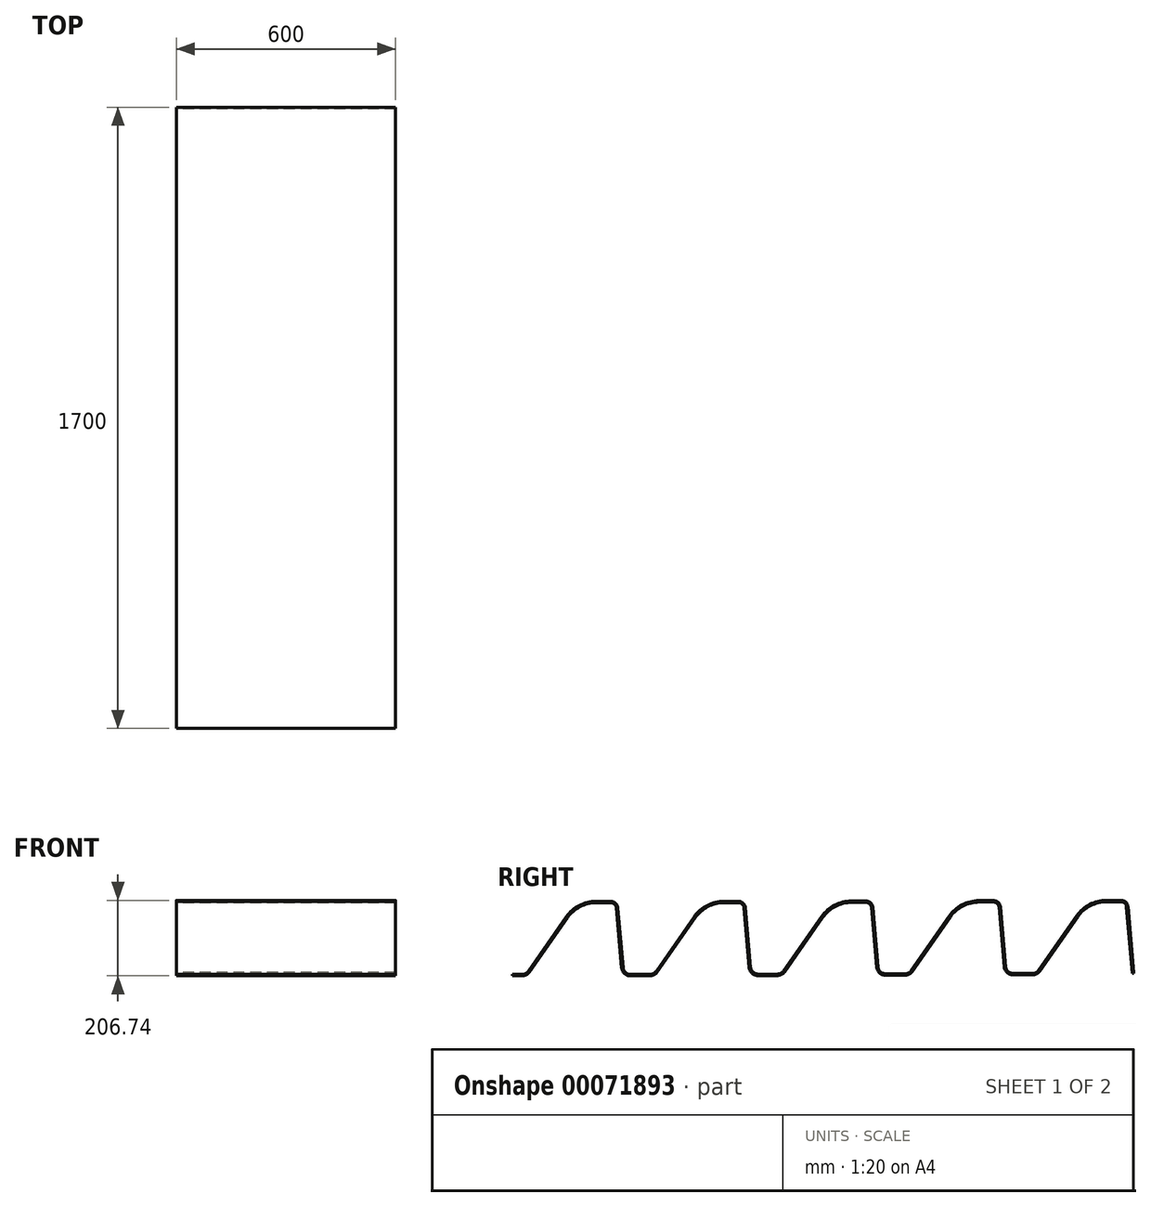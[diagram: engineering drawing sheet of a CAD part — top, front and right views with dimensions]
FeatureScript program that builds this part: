
annotation { "Feature Type Name" : "Feature", "Feature Type Description" : "" }
export const myFeature = defineFeature(function(context is Context, id is Id, definition is map)
    precondition{}
    {
        {
            var Q0;
            Q0=qCreatedBy(makeId("Right.planeOp"),FACE);
            var sketch = newSketch(context, id + "F0", { "sketchPlane" : qUnion([Q0])});
            skLineSegment(sketch, "E0", {"start": v(5.97, 8.53) * mm, "end": v(110.18, 157.36) * mm});
            skLineSegment(sketch, "E1", {"start": v(192.1, 200) * mm, "end": v(231.67, 200) * mm});
            skPoint(sketch, "E2.visualSharp", {"position": v(140.04, 200) * mm});
            skArc(sketch, "E2.filletArc", {"start": v(192.1, 200) * mm, "mid": v(145.92, 188.7) * mm, "end": v(110.18, 157.36) * mm});
            skLineSegment(sketch, "E3", {"start": v(251.6, 181.74) * mm, "end": v(265.9, 18.26) * mm});
            skPoint(sketch, "E4.visualSharp", {"position": v(250, 200) * mm});
            skArc(sketch, "E4.filletArc", {"start": v(251.6, 181.74) * mm, "mid": v(245.19, 194.75) * mm, "end": v(231.67, 200) * mm});
            skLineSegment(sketch, "E5.1.0.0", {"start": v(600.6, 182.66) * mm, "end": v(614.9, 19.17) * mm});
            skPoint(sketch, "E5.1.0.1", {"position": v(600, 200) * mm});
            skArc(sketch, "E5.1.0.2", {"start": v(542.1, 200) * mm, "mid": v(495.92, 188.7) * mm, "end": v(460.18, 157.36) * mm});
            skPoint(sketch, "E5.1.0.3", {"position": v(490.04, 200) * mm});
            skLineSegment(sketch, "E5.1.0.5", {"start": v(542.1, 200) * mm, "end": v(581.67, 200) * mm});
            skLineSegment(sketch, "E5.1.0.6", {"start": v(355.97, 8.53) * mm, "end": v(460.18, 157.36) * mm});
            skArc(sketch, "E5.1.0.7", {"start": v(600.6, 182.66) * mm, "mid": v(594.5, 195) * mm, "end": v(581.67, 200) * mm});
            skLineSegment(sketch, "E5.2.0.0", {"start": v(949.6, 183.57) * mm, "end": v(963.9, 20.08) * mm});
            skPoint(sketch, "E5.2.0.1", {"position": v(950, 200) * mm});
            skArc(sketch, "E5.2.0.2", {"start": v(891.1, 200.91) * mm, "mid": v(844.93, 189.61) * mm, "end": v(809.19, 158.27) * mm});
            skPoint(sketch, "E5.2.0.3", {"position": v(840.04, 200) * mm});
            skLineSegment(sketch, "E5.2.0.5", {"start": v(891.1, 200.91) * mm, "end": v(930.68, 200.91) * mm});
            skLineSegment(sketch, "E5.2.0.6", {"start": v(704.98, 9.44) * mm, "end": v(809.19, 158.27) * mm});
            skArc(sketch, "E5.2.0.7", {"start": v(949.6, 183.57) * mm, "mid": v(943.51, 195.92) * mm, "end": v(930.68, 200.91) * mm});
            skLineSegment(sketch, "E5.3.0.0", {"start": v(1298.6, 184.48) * mm, "end": v(1312.91, 21) * mm});
            skPoint(sketch, "E5.3.0.1", {"position": v(1300, 200) * mm});
            skArc(sketch, "E5.3.0.2", {"start": v(1240.1, 201.83) * mm, "mid": v(1193.93, 190.53) * mm, "end": v(1158.2, 159.18) * mm});
            skPoint(sketch, "E5.3.0.3", {"position": v(1190.04, 200) * mm});
            skLineSegment(sketch, "E5.3.0.5", {"start": v(1240.1, 201.83) * mm, "end": v(1279.68, 201.83) * mm});
            skLineSegment(sketch, "E5.3.0.6", {"start": v(1053.98, 10.35) * mm, "end": v(1158.2, 159.18) * mm});
            skArc(sketch, "E5.3.0.7", {"start": v(1298.6, 184.48) * mm, "mid": v(1292.52, 196.83) * mm, "end": v(1279.68, 201.83) * mm});
            skLineSegment(sketch, "E5.4.0.0", {"start": v(1647.61, 185.4) * mm, "end": v(1663.4, 5.01) * mm});
            skPoint(sketch, "E5.4.0.1", {"position": v(1650, 200) * mm});
            skArc(sketch, "E5.4.0.2", {"start": v(1589.1, 202.74) * mm, "mid": v(1542.93, 191.44) * mm, "end": v(1507.2, 160.1) * mm});
            skPoint(sketch, "E5.4.0.3", {"position": v(1540.04, 200) * mm});
            skLineSegment(sketch, "E5.4.0.5", {"start": v(1589.1, 202.74) * mm, "end": v(1628.68, 202.74) * mm});
            skLineSegment(sketch, "E5.4.0.6", {"start": v(1402.98, 11.27) * mm, "end": v(1507.2, 160.1) * mm});
            skArc(sketch, "E5.4.0.7", {"start": v(1647.61, 185.4) * mm, "mid": v(1641.52, 197.75) * mm, "end": v(1628.68, 202.74) * mm});
            skLineSegment(sketch, "E6", {"start": v(1332.84, 2.74) * mm, "end": v(1386.6, 2.74) * mm});
            skLineSegment(sketch, "E7", {"start": v(983.83, 1.83) * mm, "end": v(1037.6, 1.83) * mm});
            skLineSegment(sketch, "E8", {"start": v(634.83, 0.91) * mm, "end": v(688.6, 0.91) * mm});
            skLineSegment(sketch, "E9", {"start": v(285.82, 0) * mm, "end": v(339.59, 0) * mm});
            skLineSegment(sketch, "E10", {"start": v(-10.41, 0) * mm, "end": v(-36.6, 0) * mm});
            skPoint(sketch, "E11.visualSharp", {"position": v(267.5, 0) * mm});
            skArc(sketch, "E11.filletArc", {"start": v(265.9, 18.26) * mm, "mid": v(272.31, 5.25) * mm, "end": v(285.82, 0) * mm});
            skPoint(sketch, "E12.visualSharp", {"position": v(350, 0) * mm});
            skArc(sketch, "E12.filletArc", {"start": v(339.59, 0) * mm, "mid": v(348.82, 2.26) * mm, "end": v(355.97, 8.53) * mm});
            skPoint(sketch, "E13.visualSharp", {"position": v(616.5, 0.91) * mm});
            skArc(sketch, "E13.filletArc", {"start": v(614.9, 19.17) * mm, "mid": v(621.32, 6.17) * mm, "end": v(634.83, 0.91) * mm});
            skPoint(sketch, "E14.visualSharp", {"position": v(699, 0.91) * mm});
            skArc(sketch, "E14.filletArc", {"start": v(688.6, 0.91) * mm, "mid": v(697.83, 3.17) * mm, "end": v(704.98, 9.44) * mm});
            skPoint(sketch, "E15.visualSharp", {"position": v(965.5, 1.83) * mm});
            skArc(sketch, "E15.filletArc", {"start": v(963.9, 20.08) * mm, "mid": v(970.32, 7.08) * mm, "end": v(983.83, 1.83) * mm});
            skPoint(sketch, "E16.visualSharp", {"position": v(1048, 1.83) * mm});
            skArc(sketch, "E16.filletArc", {"start": v(1037.6, 1.83) * mm, "mid": v(1046.83, 4.09) * mm, "end": v(1053.98, 10.35) * mm});
            skPoint(sketch, "E17.visualSharp", {"position": v(1314.5, 2.74) * mm});
            skArc(sketch, "E17.filletArc", {"start": v(1312.91, 21) * mm, "mid": v(1319.32, 8) * mm, "end": v(1332.84, 2.74) * mm});
            skPoint(sketch, "E18.visualSharp", {"position": v(1397.01, 2.74) * mm});
            skArc(sketch, "E18.filletArc", {"start": v(1386.6, 2.74) * mm, "mid": v(1395.84, 5) * mm, "end": v(1402.98, 11.27) * mm});
            skPoint(sketch, "E19.visualSharp", {"position": v(0, 0) * mm});
            skArc(sketch, "E19.filletArc", {"start": v(-10.41, 0) * mm, "mid": v(-1.18, 2.26) * mm, "end": v(5.97, 8.53) * mm});
            skLineSegment(sketch, "E20.0", {"start": v(1643.63, 185.05) * mm, "end": v(1659.53, 3.3) * mm});
            skArc(sketch, "E20.1", {"start": v(1643.63, 185.05) * mm, "mid": v(1638.82, 194.8) * mm, "end": v(1628.68, 198.74) * mm});
            skLineSegment(sketch, "E20.2", {"start": v(1589.1, 198.74) * mm, "end": v(1628.68, 198.74) * mm});
            skArc(sketch, "E20.3", {"start": v(1589.1, 198.74) * mm, "mid": v(1544.78, 187.9) * mm, "end": v(1510.47, 157.8) * mm});
            skLineSegment(sketch, "E20.4", {"start": v(1406.26, 8.97) * mm, "end": v(1510.47, 157.8) * mm});
            skArc(sketch, "E20.5", {"start": v(1386.6, -1.26) * mm, "mid": v(1397.68, 1.45) * mm, "end": v(1406.26, 8.97) * mm});
            skLineSegment(sketch, "E20.6", {"start": v(1332.84, -1.26) * mm, "end": v(1386.6, -1.26) * mm});
            skArc(sketch, "E20.7", {"start": v(1308.93, 20.65) * mm, "mid": v(1316.62, 5.04) * mm, "end": v(1332.84, -1.26) * mm});
            skLineSegment(sketch, "E20.8", {"start": v(1294.62, 184.13) * mm, "end": v(1308.93, 20.65) * mm});
            skArc(sketch, "E20.9", {"start": v(1294.62, 184.13) * mm, "mid": v(1289.81, 193.88) * mm, "end": v(1279.68, 197.83) * mm});
            skLineSegment(sketch, "E20.10", {"start": v(1240.1, 197.83) * mm, "end": v(1279.68, 197.83) * mm});
            skArc(sketch, "E20.11", {"start": v(1240.1, 197.83) * mm, "mid": v(1195.78, 186.98) * mm, "end": v(1161.47, 156.89) * mm});
            skLineSegment(sketch, "E20.12", {"start": v(1057.26, 8.06) * mm, "end": v(1161.47, 156.89) * mm});
            skArc(sketch, "E20.13", {"start": v(1037.6, -2.17) * mm, "mid": v(1048.68, 0.54) * mm, "end": v(1057.26, 8.06) * mm});
            skLineSegment(sketch, "E20.14", {"start": v(983.83, -2.17) * mm, "end": v(1037.6, -2.17) * mm});
            skArc(sketch, "E20.15", {"start": v(959.92, 19.73) * mm, "mid": v(967.62, 4.13) * mm, "end": v(983.83, -2.17) * mm});
            skLineSegment(sketch, "E20.16", {"start": v(945.62, 183.22) * mm, "end": v(959.92, 19.73) * mm});
            skArc(sketch, "E20.17", {"start": v(339.59, -4) * mm, "mid": v(350.67, -1.29) * mm, "end": v(359.25, 6.23) * mm});
            skLineSegment(sketch, "E20.18", {"start": v(285.82, -4) * mm, "end": v(339.59, -4) * mm});
            skArc(sketch, "E20.19", {"start": v(261.92, 17.9) * mm, "mid": v(269.61, 2.3) * mm, "end": v(285.82, -4) * mm});
            skLineSegment(sketch, "E20.20", {"start": v(247.61, 181.4) * mm, "end": v(261.92, 17.9) * mm});
            skArc(sketch, "E20.21", {"start": v(247.61, 181.4) * mm, "mid": v(242.48, 191.8) * mm, "end": v(231.67, 196) * mm});
            skLineSegment(sketch, "E20.22", {"start": v(192.1, 196) * mm, "end": v(231.67, 196) * mm});
            skLineSegment(sketch, "E20.23", {"start": v(-10.41, -4) * mm, "end": v(-36.6, -4) * mm});
            skArc(sketch, "E20.24", {"start": v(-10.41, -4) * mm, "mid": v(0.67, -1.29) * mm, "end": v(9.25, 6.23) * mm});
            skLineSegment(sketch, "E20.25", {"start": v(9.25, 6.23) * mm, "end": v(113.46, 155.06) * mm});
            skArc(sketch, "E20.26", {"start": v(192.1, 196) * mm, "mid": v(147.77, 185.15) * mm, "end": v(113.46, 155.06) * mm});
            skLineSegment(sketch, "E20.27", {"start": v(359.25, 6.23) * mm, "end": v(463.46, 155.06) * mm});
            skArc(sketch, "E20.28", {"start": v(542.1, 196) * mm, "mid": v(497.77, 185.15) * mm, "end": v(463.46, 155.06) * mm});
            skLineSegment(sketch, "E20.29", {"start": v(542.1, 196) * mm, "end": v(581.67, 196) * mm});
            skArc(sketch, "E20.30", {"start": v(596.62, 182.3) * mm, "mid": v(591.8, 192.06) * mm, "end": v(581.67, 196) * mm});
            skLineSegment(sketch, "E20.31", {"start": v(596.62, 182.3) * mm, "end": v(610.92, 18.82) * mm});
            skArc(sketch, "E20.32", {"start": v(610.92, 18.82) * mm, "mid": v(618.61, 3.22) * mm, "end": v(634.83, -3.09) * mm});
            skLineSegment(sketch, "E20.33", {"start": v(634.83, -3.09) * mm, "end": v(688.6, -3.09) * mm});
            skArc(sketch, "E20.34", {"start": v(688.6, -3.09) * mm, "mid": v(699.67, -0.38) * mm, "end": v(708.25, 7.15) * mm});
            skLineSegment(sketch, "E20.35", {"start": v(708.25, 7.15) * mm, "end": v(812.46, 155.98) * mm});
            skArc(sketch, "E20.36", {"start": v(891.1, 196.91) * mm, "mid": v(846.77, 186.07) * mm, "end": v(812.46, 155.98) * mm});
            skLineSegment(sketch, "E20.37", {"start": v(891.1, 196.91) * mm, "end": v(930.68, 196.91) * mm});
            skArc(sketch, "E20.38", {"start": v(945.62, 183.22) * mm, "mid": v(940.81, 192.97) * mm, "end": v(930.68, 196.91) * mm});
            skLineSegment(sketch, "E21", {"start": v(-36.6, 0) * mm, "end": v(-36.6, -4) * mm});
            skLineSegment(sketch, "E22", {"start": v(1659.53, 3.3) * mm, "end": v(1663.4, 3.3) * mm});
            skLineSegment(sketch, "E23", {"start": v(1663.4, 5.01) * mm, "end": v(1663.4, 3.3) * mm});
            skSolve(sketch);
        }
        {
            var Q0;
            Q0 = qSketchRegion(id + "F0", true);
            extrude(context, id + "F1", {"entities" : qUnion([Q0]), "depth" : 300 * mm, "hasSecondDirection" : true, "secondDirectionOppositeDirection" : true, "secondDirectionDepth" : 300 * mm});
        }
    });
